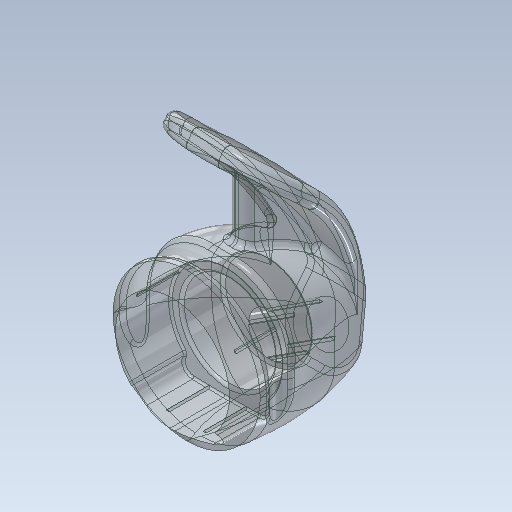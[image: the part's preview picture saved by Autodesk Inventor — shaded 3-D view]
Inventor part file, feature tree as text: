
AUTODESK INVENTOR PART (.ipt)
format: ipt  version: 2020 (Build 240168000, 168)  size: 1,328,640 bytes
history: native  units: in
note: dims shown in document units (in); Inventor stores cm internally (conversion verified against a paired STEP export)
features: sketch x12, extrude x10, plane x3, draft x2, fillet x2, chamfer x1, sweep x1, hole x1
ambient origin geometry x7: Origin, XZ Plane, XY Plane, X Axis, Y Axis, Z Axis, Center Point
bodies: Solid1 (feature_tree)
feature tree (32):
  plane  "Work Plane7"
  plane  "Work Plane9"
  extrude  "ExtrusionMidplane1"  TaperAngle=0.0deg  [1 undecoded]
  extrude  "Extrusion13"  TaperAngle=0.0deg  [1 undecoded]
  chamfer  "Chamfer3"  Distance=0.13in
  sketch  "Sketch7-<F>"  dims[d2=0.16in d3=0.0in d5=0.0in]
  extrude  "ExtrusionMidThru2"  Depth=0.03in
  sketch  "Sketch3-<F>"  dims[d6=0.0in d7=0.0in d24=0.13in d25=0.0in]
  plane  "Work Plane8"
  sweep  "SweepPathOnly1"
  extrude  "ExtrusionMidplane2"  TaperAngle=0.0deg  [1 undecoded]
  draft  "FaceDraft1"
  draft  "FaceDraft2"
  extrude  "Extrusion14"  Depth=0.15in
  extrude  "ExtrusionBlind3"  Depth=0.0137in
  fillet  "Fillet45"  Radius=0.115in
  extrude  "ExtrusionBlind8"  Depth=0.04in
  extrude  "ExtrusionToExtFace1"  Depth=0.5in
  extrude  "ExtrusionBlind9"  TaperAngle=0.0deg  [1 undecoded]
  hole  "Hole1"  [1 undecoded]
  fillet  "Fillet46"  Radius=0.045in
  extrude  "ExtrusionBlind10"  Depth=0.003in
  sketch  "Sketch2-<F>"  dims[d26=0.25in d27=0.03in d28=0.081in]
  sketch  "Sketch8-<F>"  dims[d29=0.03in d30=0.081in d31=0.081in d32=0.04in]
  sketch  "Sketch9-<F>"  dims[d33=0.081in d34=0.04in d35=0.0in]
  sketch  "Sketch11-<U>"  dims[d36=0.007in d37=0.15in d38=-0.0137in]
  sketch  "Sketch12-<F>"  dims[d39=0.0137in d40=0.0137in d45=0.115in d46=0.0in]
  sketch  "Sketch13-<F>"  dims[d47=0.06in d48=0.04in]
  sketch  "Sketch14-<F>"  dims[d49=0.0685in d50=0.0in d51=0.5in]
  sketch  "Sketch15-<F>"  dims[d52=0.0in d53=0.0in]
  sketch  "Sketch16-<F>"  dims[d54=0.13in d55=0.0in d56=0.045in d57=0.0in]
  sketch  "Sketch17-<F>"  dims[d58=0.044in d59=0.75in d60=0.375in d61=0.25in d62=0.5635in d63=0.015in d64=90.0deg d65=0.045in d66=0.0in d67=0.003in d70=0.01in d71=0.006in d72=0.006in d73=0.025in d74=0.006in d77=0.0in d78=0.154in d79=0.0725in d80=0.161in d81=0.1405in d82=0.7524in d83=0.287in d84=0.15in d85=0.063in d87=0.12in d88=0.025in d89=0.0in d90=0.021in d91=0.018in d92=45.0deg d93=0.022in d94=0.088in d95=0.0526in d96=0.03in d97=0.3405in d98=0.3195in d99=0.0075in d100=0.1065in d103=0.007in d104=0.0465in d105=0.0in d106=0.0in d107=0.5in d108=0.062in d109=0.0115in d110=0.004in d113=0.0725in d114=0.05in d115=1.2265in d117=0.079in d118=0.045in d119=0.02in d121=0.025in d122=0.0335in d123=0.1in d126=0.04in d127=0.02in d128=0.06in d129=120.0deg d130=0.002in]
note: 5 required parameter values undecoded (feature->parameter linkage not recoverable at this tier; creation-order binding heuristic only, values carry confidence <= 0.55)
